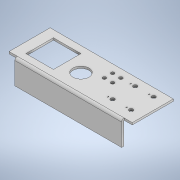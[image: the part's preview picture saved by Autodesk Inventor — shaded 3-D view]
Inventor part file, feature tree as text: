
AUTODESK INVENTOR PART (.ipt)
format: ipt  version: 2021.3 (Build 253353010, 353A)  size: 201,728 bytes
history: native  units: in
note: dims shown in document units (in); Inventor stores cm internally (conversion verified against a paired STEP export)
features: sketch x3, extrude x2, other x1
ambient origin geometry x8: Origin, YZ Plane, XZ Plane, XY Plane, X Axis, Y Axis, Z Axis, Center Point
bodies: Solid1 (feature_tree)
feature tree (6):
  extrude  "Extrusion1"  Depth=3.937in
  extrude  "Extrusion2"  Depth=0.7874in
  other  "Bend Part2"
  sketch  "Sketch1"  dims[d0=3.937in d1=2.1654in]
  sketch  "Sketch2"  dims[d2=11.811in d3=0.7874in]
  sketch  "Sketch3"  dims[d4=0.7874in d5=5.9055in d6=1.9685in d7=0.1969in d8=0.0in d11=2.6378in d12=2.6378in d13=0.6693in d15=0.9843in d16=1.5354in d17=1.5748in d18=1.5748in d19=1.2598in d20=1.2598in d23=0.6299in d24=0.6299in d25=0.1181in d26=0.1181in d27=0.1181in d28=0.1181in d29=0.374in d30=1.7717in d31=2.1654in d32=0.7874in d34=0.3268in d36=0.7874in d37=0.7874in d38=0.7874in d39=1.5748in d40=1.378in d41=0.4331in d42=0.1024in d43=0.0512in d44=0.1024in d45=0.0512in d46=0.1024in d47=0.0512in d48=0.1024in d49=0.0512in d50=0.4331in d51=0.0in d52=0.0in d53=0.0394in d54=90.0deg]
